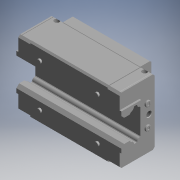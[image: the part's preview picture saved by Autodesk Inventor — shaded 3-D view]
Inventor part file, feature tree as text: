
AUTODESK INVENTOR PART (.ipt)
format: ipt  version: 2022 (Build 260153000, 153)  size: 431,104 bytes
history: native  units: mm (DEFAULTED — no unit token found)
features: sketch x39, extrude x22, other x21, revolve x10, hole x7, pattern_linear x1
ambient origin geometry x8: Origin, YZ Plane, XZ Plane, XY Plane, X Axis, Y Axis, Z Axis, Center Point
bodies: Solid1 (feature_tree)
feature tree (100):
  extrude  "Extrusion1"  Depth=2.0mm
  hole  "Hole1"  [1 undecoded]
  pattern_linear  "Rectangular Pattern1"  [2 undecoded]
  extrude  "Extrusion2"  [1 undecoded]
  extrude  "Extrusion3"  [1 undecoded]
  extrude  "Extrusion4"  [1 undecoded]
  extrude  "Extrusion5"  [1 undecoded]
  extrude  "Extrusion6"  [1 undecoded]
  extrude  "Extrusion7"  [1 undecoded]
  hole  "Hole2"  [1 undecoded]
  hole  "Hole3"  [1 undecoded]
  extrude  "Extrusion8"  [1 undecoded]
  extrude  "Extrusion9"  [1 undecoded]
  extrude  "Extrusion10"  [1 undecoded]
  extrude  "Extrusion11"  [1 undecoded]
  extrude  "Extrusion12"  [1 undecoded]
  revolve  "Revolution1"  [1 undecoded]
  revolve  "Revolution2"  [1 undecoded]
  revolve  "Revolution3"  [1 undecoded]
  revolve  "Revolution4"  [1 undecoded]
  extrude  "Extrusion13"  [1 undecoded]
  extrude  "Extrusion14"  [1 undecoded]
  extrude  "Extrusion15"  [1 undecoded]
  extrude  "Extrusion16"  [1 undecoded]
  extrude  "Extrusion17"  [1 undecoded]
  extrude  "Extrusion18"  [1 undecoded]
  extrude  "Extrusion19"  [1 undecoded]
  extrude  "Extrusion20"  [1 undecoded]
  extrude  "Extrusion21"  [1 undecoded]
  extrude  "Extrusion22"  [1 undecoded]
  hole  "Hole4"  [1 undecoded]
  hole  "Hole5"  [1 undecoded]
  revolve  "Revolution5"  [1 undecoded]
  revolve  "Revolution6"  [1 undecoded]
  revolve  "Revolution7"  [1 undecoded]
  revolve  "Revolution8"  [1 undecoded]
  revolve  "Revolution9"  [1 undecoded]
  hole  "Hole6"  [1 undecoded]
  revolve  "Revolution10"  [1 undecoded]
  hole  "Hole7"  [1 undecoded]
  other  "4TRACK_XY"
  other  "4TRACK_YZ"
  other  "4TRACK_ZX"
  other  "4TRACK_X"
  other  "4TRACK_Y"
  other  "4TRACK_Z"
  other  "4TRACK_Center"
  other  "niple_XY"
  other  "niple_YZ"
  other  "niple_ZX"
  other  "niple_X"
  other  "niple_Y"
  other  "niple_Z"
  other  "niple_Center"
  other  "niple2_XY"
  other  "niple2_YZ"
  other  "niple2_ZX"
  other  "niple2_X"
  other  "niple2_Y"
  other  "niple2_Z"
  other  "niple2_Center"
  sketch  "Sketch_22"  dims[d53=360.0deg]
  sketch  "Sketch2"  dims[d2=6.647mm d3=12.6765mm d4=8.0mm d5=2.0mm d6=90.0deg d7=14.4mm d8=120.0deg d9=20.0mm d11=50.0mm d12=20.0mm d14=50.0mm]
  sketch  "Sketch_7"  dims[d23=10.5mm d24=0.0mm]
  sketch  "Sketch_2"  dims[d15=11.0mm d16=0.0mm d17=3.5mm d18=0.0mm]
  sketch  "Sketch_8"  dims[d25=10.5mm d26=0.0mm]
  sketch  "Sketch_42"  dims[d82=4.917mm d83=5.5415mm d84=6.0mm d85=2.0mm d86=90.0deg d87=6.0mm d88=120.0deg]
  sketch  "Sketch_106"  dims[d102=5.2mm d103=6.0mm d104=4.0mm d105=2.0mm d106=90.0deg d107=5.2mm d108=0.0mm]
  sketch  "Sketch_107"  dims[d109=0.0mm d110=0.0mm]
  sketch  "Sketch9"  dims[d27=6.2mm d28=6.0mm d29=4.0mm d30=2.0mm d31=90.0deg d32=1.0mm d33=0.0mm]
  sketch  "Sketch10"  dims[d34=6.2mm d35=6.0mm d36=4.0mm d37=2.0mm d38=90.0deg d39=1.0mm d40=0.0mm]
  sketch  "Sketch_1"  dims[d0=80.4mm d1=0.0mm]
  sketch  "Sketch_6"  dims[d21=3.5mm d22=0.0mm]
  sketch  "Sketch_20"  dims[d51=360.0deg]
  sketch  "Sketch_21"  dims[d52=360.0deg]
  sketch  "Sketch_65"  dims[d93=360.0deg]
  sketch  "Sketch_4"  dims[d19=11.0mm d20=0.0mm]
  sketch  "Sketch_14"  dims[d45=2.0mm d46=0.0mm]
  sketch  "Sketch_15"  dims[d47=2.0mm d48=0.0mm]
  sketch  "Sketch_16"  dims[d49=109.4mm d50=0.0mm]
  sketch  "Sketch_24"  dims[d54=360.0deg]
  sketch  "Sketch_25"  dims[d55=0.75mm d56=0.0mm]
  sketch  "Sketch_26"  dims[d57=0.75mm d58=0.0mm]
  sketch  "Sketch_27"  dims[d59=0.75mm d60=0.0mm]
  sketch  "Sketch_12"  dims[d41=2.0mm d42=0.0mm]
  sketch  "Sketch_13"  dims[d43=2.0mm d44=0.0mm]
  sketch  "Sketch_45"  dims[d89=360.0deg]
  sketch  "Sketch_46"  dims[d90=360.0deg]
  sketch  "Sketch_47"  dims[d91=360.0deg]
  sketch  "Sketch_48"  dims[d92=360.0deg]
  sketch  "Sketch30"  dims[d61=0.75mm d62=0.0mm]
  sketch  "Sketch31"  dims[d63=68.0mm d64=0.0mm]
  sketch  "Sketch_34"  dims[d65=68.0mm d66=0.0mm]
  sketch  "Sketch_35"  dims[d67=47.5mm d68=0.0mm]
  sketch  "Sketch_37"  dims[d69=47.5mm d70=0.0mm]
  sketch  "Sketch_38"  dims[d73=47.5mm d74=0.0mm]
  sketch  "Sketch_94"  dims[d94=5.2mm d95=6.0mm d96=4.0mm d97=2.0mm d98=90.0deg d99=5.2mm d100=0.0mm]
  sketch  "Sketch37"  dims[d71=47.5mm d72=0.0mm]
  sketch  "Sketch_96"  dims[d101=360.0deg]
  sketch  "Sketch39"  dims[d75=4.917mm d76=5.5415mm d77=6.0mm d78=2.0mm d79=90.0deg d80=6.0mm d81=120.0deg]
note: 40 required parameter values undecoded (feature->parameter linkage not recoverable at this tier; creation-order binding heuristic only, values carry confidence <= 0.55)
